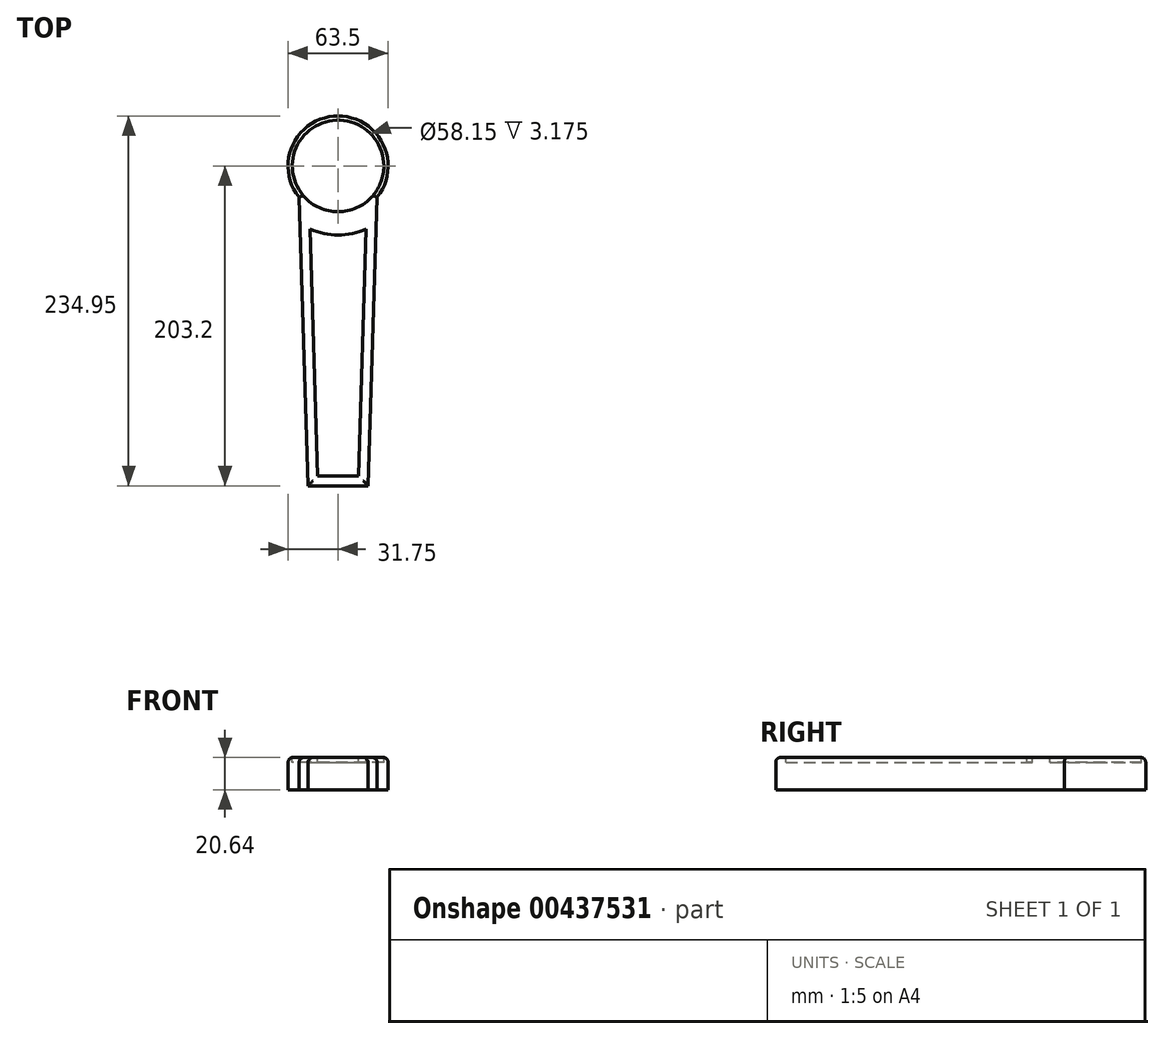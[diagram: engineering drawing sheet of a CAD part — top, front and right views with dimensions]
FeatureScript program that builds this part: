
annotation { "Feature Type Name" : "Feature", "Feature Type Description" : "" }
export const myFeature = defineFeature(function(context is Context, id is Id, definition is map)
    precondition{}
    {
        {
            var Q0;
            Q0=qCreatedBy(makeId("Top.planeOp"),FACE);
            var sketch = newSketch(context, id + "F0", { "sketchPlane" : qUnion([Q0])});
            skCircle(sketch, "E0", {"center": v(0, 0) * mm, "radius": 31.75 * mm});
            skSolve(sketch);
        }
        {
            var Q0;
            Q0=qSketchRegion(id+"F0",true);
            extrude(context, id + "F1", {"entities" : qUnion([Q0]), "depth" : 20.64 * mm});
        }
        {
            var Q0;
            Q0=makeQuery(id+"F1.opExtrude","CAP_FACE",FACE,{"disambiguationData":[OSD([sQuery(id+"F0.wireOp",EDGE,"E0")])],"isStart":false});
            var sketch = newSketch(context, id + "F2", { "sketchPlane" : qUnion([Q0])});
            skCircle(sketch, "E1", {"center": v(0, 0) * mm, "radius": 29.07 * mm});
            skSolve(sketch);
        }
        {
            var Q0;
            Q0=qSketchRegion(id+"F2",true);
            extrude(context, id + "F3", {"entities" : qUnion([Q0]), "operationType" : NewBodyOperationType.REMOVE, "oppositeDirection" : true, "depth" : 3.17 * mm});
        }
        {
            var Q0;
            Q0=qCreatedBy(makeId("Top.planeOp"),FACE);
            var sketch = newSketch(context, id + "F4", { "sketchPlane" : qUnion([Q0])});
            skLineSegment(sketch, "E2.bottom", {"start": v(-25.4, 0) * mm, "end": v(25.4, 0) * mm});
            skLineSegment(sketch, "E2.top", {"start": v(-19.05, -203.2) * mm, "end": v(19.05, -203.2) * mm});
            skPoint(sketch, "E2.middle", {"position": v(0, -101.6) * mm});
            skPoint(sketch, "E3", {"position": v(-19.05, -203.2) * mm});
            skPoint(sketch, "E4", {"position": v(19.05, -203.2) * mm});
            skLineSegment(sketch, "E5", {"start": v(-25.4, 0) * mm, "end": v(-19.05, -203.2) * mm});
            skLineSegment(sketch, "E6", {"start": v(19.05, -203.2) * mm, "end": v(25.4, 0) * mm});
            skPoint(sketch, "E7.orphan", {"position": v(-25.4, -203.2) * mm});
            skPoint(sketch, "E8.orphan", {"position": v(25.4, -203.2) * mm});
            skSolve(sketch);
        }
        {
            var Q0;
            Q0 = qSketchRegion(id + "F4", true);
            extrude(context, id + "F5", {"entities" : qUnion([Q0]), "operationType" : NewBodyOperationType.ADD, "depth" : 17.46 * mm});
        }
        {
            var Q0;
            Q0=makeQuery(id+"F5.opExtrude","CAP_FACE",FACE,{"disambiguationData":[OSD([sQuery(id+"F4.wireOp",EDGE,"E2.bottom"),sQuery(id+"F4.wireOp",EDGE,"E2.top"),sQuery(id+"F4.wireOp",EDGE,"E5"),sQuery(id+"F4.wireOp",EDGE,"E6")])],"isStart":false});
            var sketch = newSketch(context, id + "F6", { "sketchPlane" : qUnion([Q0])});
            skLineSegment(sketch, "E9", {"start": v(-19.05, -203.2) * mm, "end": v(-24.63, -24.77) * mm});
            skLineSegment(sketch, "E10", {"start": v(24.63, -24.77) * mm, "end": v(19.05, -203.2) * mm});
            skLineSegment(sketch, "E11", {"start": v(19.05, -203.2) * mm, "end": v(-19.05, -203.2) * mm});
            skArc(sketch, "E12", {"start": v(-24.63, -24.77) * mm, "mid": v(0, -34.93) * mm, "end": v(24.63, -24.77) * mm});
            skLineSegment(sketch, "E13", {"start": v(-24.63, -24.77) * mm, "end": v(-24.78, -19.85) * mm});
            skLineSegment(sketch, "E14", {"start": v(-24.78, -19.85) * mm, "end": v(-21.49, -19.85) * mm});
            skLineSegment(sketch, "E15", {"start": v(24.78, -19.85) * mm, "end": v(24.63, -24.77) * mm});
            skArc(sketch, "E16", {"start": v(-21.49, -19.85) * mm, "mid": v(0, -29.25) * mm, "end": v(21.49, -19.85) * mm});
            skLineSegment(sketch, "E17.trimOffspring", {"start": v(21.49, -19.85) * mm, "end": v(24.78, -19.85) * mm});
            skSolve(sketch);
        }
        {
            var Q0;
            Q0 = qSketchRegion(id + "F6", true);
            extrude(context, id + "F7", {"entities" : qUnion([Q0]), "operationType" : NewBodyOperationType.ADD, "depth" : 3.17 * mm});
        }
        {
            var Q0;
            Q0=makeQuery(id+"F7.opExtrude","CAP_FACE",FACE,{"disambiguationData":[OSD([sQuery(id+"F6.wireOp",EDGE,"E9"),sQuery(id+"F6.wireOp",EDGE,"E10"),sQuery(id+"F6.wireOp",EDGE,"E11"),sQuery(id+"F6.wireOp",EDGE,"E12")])],"isStart":false});
            var sketch = newSketch(context, id + "F8", { "sketchPlane" : qUnion([Q0])});
            skLineSegment(sketch, "E18.0", {"start": v(12.9, -196.85) * mm, "end": v(17.8, -40.04) * mm});
            skLineSegment(sketch, "E18.1", {"start": v(-12.9, -196.85) * mm, "end": v(12.9, -196.85) * mm});
            skLineSegment(sketch, "E18.2", {"start": v(-17.8, -40.04) * mm, "end": v(-12.9, -196.85) * mm});
            skArc(sketch, "E18.3", {"start": v(17.8, -40.04) * mm, "mid": v(0, -43.82) * mm, "end": v(-17.8, -40.04) * mm});
            skSolve(sketch);
        }
        {
            var Q0;
            Q0 = qSketchRegion(id + "F8", true);
            extrude(context, id + "F9", {"entities" : qUnion([Q0]), "operationType" : NewBodyOperationType.REMOVE, "oppositeDirection" : true, "depth" : 3.17 * mm});
        }
        {
            var Q0;
            Q0=makeQuery(id+"F7.opExtrude","CAP_EDGE",EDGE,{"disambiguationData":[OSD([sQuery(id+"F6.wireOp",EDGE,"E9")])],"isStart":false});
            var Q1;
            Q1=makeQuery(id+"F7.opExtrude","CAP_EDGE",EDGE,{"disambiguationData":[OSD([sQuery(id+"F6.wireOp",EDGE,"E11")])],"isStart":false});
            var Q2;
            Q2=makeQuery(id+"F7.opExtrude","CAP_EDGE",EDGE,{"disambiguationData":[OSD([sQuery(id+"F6.wireOp",EDGE,"E10")])],"isStart":false});
            fillet(context, id + "F10", {"entities" : qUnion([Q0, Q1, Q2]), "radius" : 3.17 * mm, "tangentPropagation" : true, "allowEdgeOverflow" : false});
        }
        {
            var Q0;
            Q0=makeQuery(id+"F1.opExtrude","CAP_EDGE",EDGE,{"disambiguationData":[OSD([sQuery(id+"F0.wireOp",EDGE,"E0")])],"isStart":false});
            fillet(context, id + "F11", {"entities" : qUnion([Q0]), "radius" : 3.17 * mm, "tangentPropagation" : true, "allowEdgeOverflow" : false});
        }
    });
